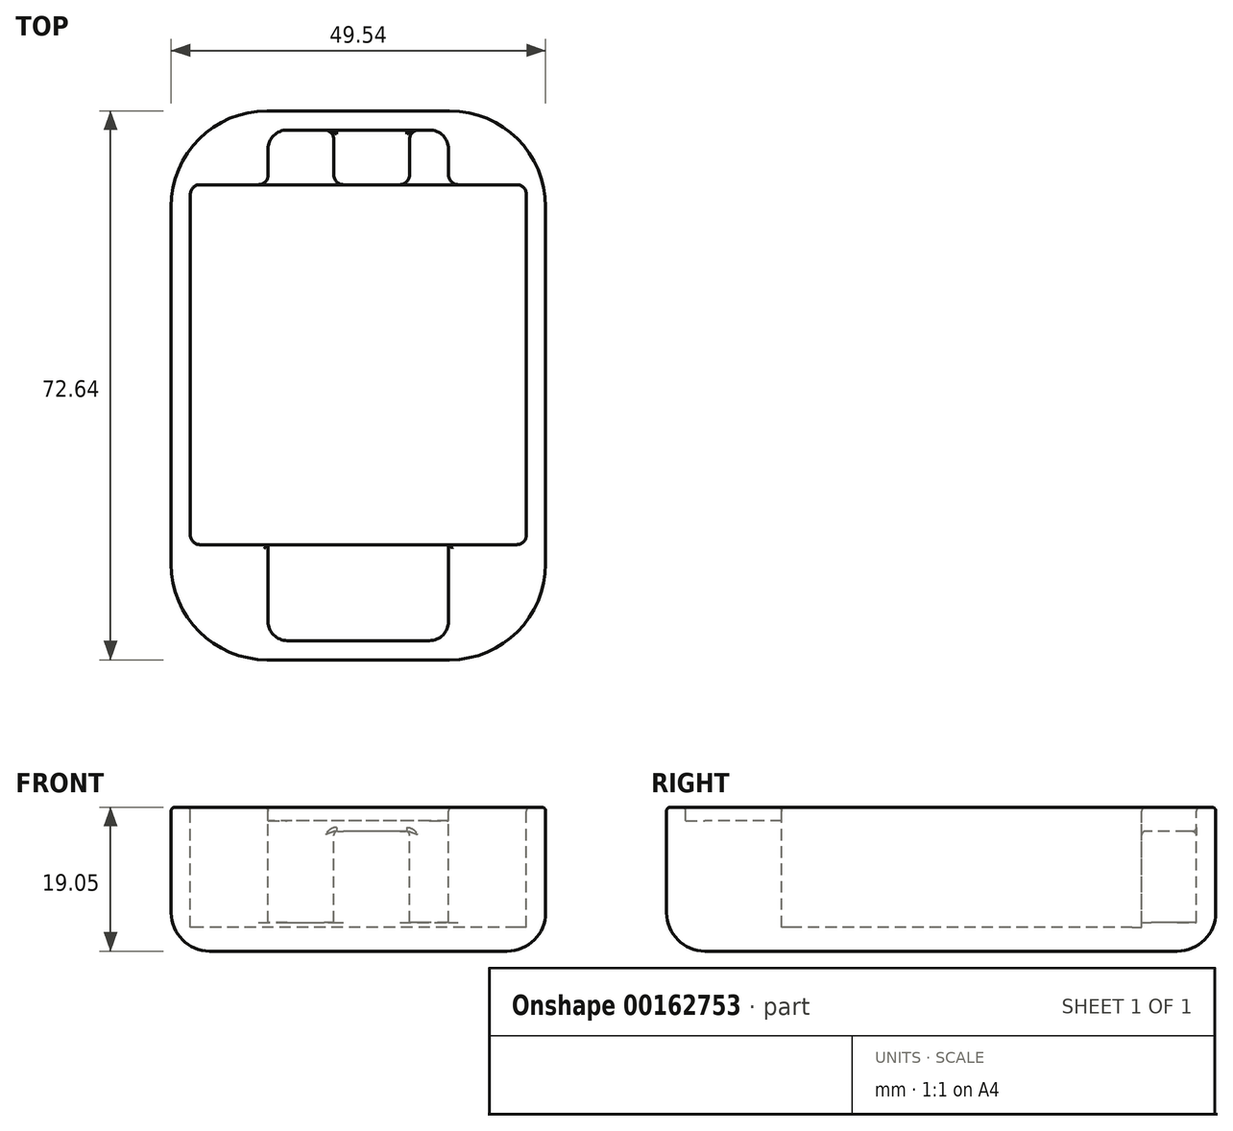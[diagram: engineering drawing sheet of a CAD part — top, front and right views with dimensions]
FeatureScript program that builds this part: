
annotation { "Feature Type Name" : "Feature", "Feature Type Description" : "" }
export const myFeature = defineFeature(function(context is Context, id is Id, definition is map)
    precondition{}
    {
        {
            var Q0;
            Q0=qCreatedBy(makeId("Top.planeOp"),FACE);
            var sketch = newSketch(context, id + "F0", { "sketchPlane" : qUnion([Q0])});
            skLineSegment(sketch, "E0.bottom", {"start": v(11.94, 33.78) * mm, "end": v(-11.94, 33.78) * mm});
            skLineSegment(sketch, "E0.top", {"start": v(11.94, -33.78) * mm, "end": v(-11.94, -33.78) * mm});
            skLineSegment(sketch, "E0.left", {"start": v(11.94, 33.78) * mm, "end": v(11.94, -33.78) * mm});
            skLineSegment(sketch, "E0.right", {"start": v(-11.94, 33.78) * mm, "end": v(-11.94, -33.78) * mm});
            skPoint(sketch, "E0.middle", {"position": v(0, 0) * mm});
            skLineSegment(sketch, "E1.bottom", {"start": v(22.22, 26.54) * mm, "end": v(-22.23, 26.54) * mm});
            skLineSegment(sketch, "E1.top", {"start": v(22.23, -21.08) * mm, "end": v(-22.22, -21.08) * mm});
            skLineSegment(sketch, "E1.left", {"start": v(22.23, 26.54) * mm, "end": v(22.23, -21.08) * mm});
            skLineSegment(sketch, "E1.right", {"start": v(-22.23, 26.54) * mm, "end": v(-22.23, -21.08) * mm});
            skPoint(sketch, "E1.middle", {"position": v(0, 2.73) * mm});
            skLineSegment(sketch, "E2.bottom", {"start": v(24.76, 36.32) * mm, "end": v(-24.77, 36.32) * mm});
            skLineSegment(sketch, "E2.top", {"start": v(24.77, -36.32) * mm, "end": v(-24.76, -36.32) * mm});
            skLineSegment(sketch, "E2.left", {"start": v(24.76, 36.32) * mm, "end": v(24.77, -36.32) * mm});
            skLineSegment(sketch, "E2.right", {"start": v(-24.77, 36.32) * mm, "end": v(-24.76, -36.32) * mm});
            skSolve(sketch);
        }
        {
            var Q0;
            {var subQ10=sQuery(id+"F0.wireOp",EDGE,"E0.bottom");Q0=makeQuery(id+"F0.imprint","IMPRINT",FACE,{"disambiguationData":[TD([[makeQuery(id+"F0.imprint","IMPRINT",EDGE,{"derivedFrom":subQ10}),-1.0]])]});}
            var Q1;
            {var subQ0=sQuery(id+"F0.wireOp",EDGE,"E0.bottom");Q1=makeQuery(id+"F0.imprint","IMPRINT",FACE,{"disambiguationData":[TD([[makeQuery(id+"F0.imprint","IMPRINT",EDGE,{"derivedFrom":subQ0}),1.0]])]});}
            var Q2;
            {var subQ5=sQuery(id+"F0.wireOp",EDGE,"E1.right");Q2=makeQuery(id+"F0.imprint","IMPRINT",FACE,{"disambiguationData":[TD([[makeQuery(id+"F0.imprint","IMPRINT",EDGE,{"derivedFrom":subQ5}),1.0]])]});}
            var Q3;
            {var subQ0=sQuery(id+"F0.wireOp",EDGE,"E1.bottom");var subQ1=sQuery(id+"F0.wireOp",EDGE,"E0.left");var subQ2=makeQuery(id+"F0.imprint","INTERSECT",VERTEX,{"derivedFrom":[subQ1,subQ0]});Q3=makeQuery(id+"F0.imprint","IMPRINT",FACE,{"disambiguationData":[TD([[makeQuery(id+"F0.imprint","IMPRINT",EDGE,{"disambiguationData":[TD([[subQ2,-1.0]])],"derivedFrom":subQ1}),-1.0]])]});}
            var Q4;
            {var subQ5=sQuery(id+"F0.wireOp",EDGE,"E1.left");Q4=makeQuery(id+"F0.imprint","IMPRINT",FACE,{"disambiguationData":[TD([[makeQuery(id+"F0.imprint","IMPRINT",EDGE,{"derivedFrom":subQ5}),-1.0]])]});}
            var Q5;
            {var subQ0=sQuery(id+"F0.wireOp",EDGE,"E0.top");Q5=makeQuery(id+"F0.imprint","IMPRINT",FACE,{"disambiguationData":[TD([[makeQuery(id+"F0.imprint","IMPRINT",EDGE,{"derivedFrom":subQ0}),-1.0]])]});}
            var Q6;
            Q6=sQuery(id+"F0.wireOp",EDGE,"E2.bottom");
            var Q7;
            Q7=sQuery(id+"F0.wireOp",EDGE,"E2.right");
            var Q8;
            Q8=sQuery(id+"F0.wireOp",EDGE,"E2.left");
            var Q9;
            Q9=sQuery(id+"F0.wireOp",EDGE,"E2.top");
            extrude(context, id + "F1", {"entities" : qUnion([Q0, Q1, Q2, Q3, Q4, Q5]), "surfaceEntities" : qUnion([Q6, Q7, Q8, Q9]), "oppositeDirection" : true, "depth" : 19.05 * mm});
        }
        {
            var Q0;
            {var subQ5=sQuery(id+"F0.wireOp",EDGE,"E1.right");Q0=makeQuery(id+"F0.imprint","IMPRINT",FACE,{"disambiguationData":[TD([[makeQuery(id+"F0.imprint","IMPRINT",EDGE,{"derivedFrom":subQ5}),1.0]])]});}
            var Q1;
            {var subQ0=sQuery(id+"F0.wireOp",EDGE,"E1.bottom");var subQ1=sQuery(id+"F0.wireOp",EDGE,"E0.left");var subQ2=makeQuery(id+"F0.imprint","INTERSECT",VERTEX,{"derivedFrom":[subQ1,subQ0]});Q1=makeQuery(id+"F0.imprint","IMPRINT",FACE,{"disambiguationData":[TD([[makeQuery(id+"F0.imprint","IMPRINT",EDGE,{"disambiguationData":[TD([[subQ2,-1.0]])],"derivedFrom":subQ1}),-1.0]])]});}
            var Q2;
            {var subQ5=sQuery(id+"F0.wireOp",EDGE,"E1.left");Q2=makeQuery(id+"F0.imprint","IMPRINT",FACE,{"disambiguationData":[TD([[makeQuery(id+"F0.imprint","IMPRINT",EDGE,{"derivedFrom":subQ5}),-1.0]])]});}
            extrude(context, id + "F2", {"entities" : qUnion([Q0, Q1, Q2]), "operationType" : NewBodyOperationType.REMOVE, "oppositeDirection" : true, "depth" : 15.88 * mm});
        }
        {
            var Q0;
            {var subQ0=sQuery(id+"F0.wireOp",EDGE,"E0.bottom");Q0=makeQuery(id+"F0.imprint","IMPRINT",FACE,{"disambiguationData":[TD([[makeQuery(id+"F0.imprint","IMPRINT",EDGE,{"derivedFrom":subQ0}),1.0]])]});}
            var Q1;
            {var subQ0=sQuery(id+"F0.wireOp",EDGE,"E0.top");Q1=makeQuery(id+"F0.imprint","IMPRINT",FACE,{"disambiguationData":[TD([[makeQuery(id+"F0.imprint","IMPRINT",EDGE,{"derivedFrom":subQ0}),-1.0]])]});}
            extrude(context, id + "F3", {"entities" : qUnion([Q0, Q1]), "operationType" : NewBodyOperationType.REMOVE, "oppositeDirection" : true, "depth" : 1.78 * mm});
        }
        {
            var Q0;
            {var subQ0=sQuery(id+"F0.wireOp",EDGE,"E0.bottom");Q0=makeQuery(id+"F0.imprint","IMPRINT",FACE,{"disambiguationData":[TD([[makeQuery(id+"F0.imprint","IMPRINT",EDGE,{"derivedFrom":subQ0}),1.0]])]});}
            extrude(context, id + "F4", {"entities" : qUnion([Q0]), "operationType" : NewBodyOperationType.REMOVE, "oppositeDirection" : true, "depth" : 3.17 * mm});
        }
        {
            var Q0;
            {var subQ0=sQuery(id+"F0.wireOp",EDGE,"E1.bottom");var subQ1=sQuery(id+"F0.wireOp",EDGE,"E0.left");var subQ2=makeQuery(id+"F0.imprint","INTERSECT",VERTEX,{"derivedFrom":[subQ1,subQ0]});Q0=makeQuery(id+"F0.imprint","IMPRINT",FACE,{"disambiguationData":[TD([[makeQuery(id+"F0.imprint","IMPRINT",EDGE,{"disambiguationData":[TD([[subQ2,-1.0]])],"derivedFrom":subQ1}),-1.0]])]});}
            var sketch = newSketch(context, id + "F5", { "sketchPlane" : qUnion([Q0])});
            skLineSegment(sketch, "E3.bottom", {"start": v(-11.94, 33.78) * mm, "end": v(-3.24, 33.78) * mm});
            skLineSegment(sketch, "E3.top", {"start": v(-11.94, 18.88) * mm, "end": v(-3.24, 18.88) * mm});
            skLineSegment(sketch, "E3.left", {"start": v(-11.94, 33.78) * mm, "end": v(-11.94, 18.88) * mm});
            skLineSegment(sketch, "E3.right", {"start": v(-3.24, 33.78) * mm, "end": v(-3.24, 18.88) * mm});
            skLineSegment(sketch, "E4.bottom", {"start": v(11.94, 33.78) * mm, "end": v(6.76, 33.78) * mm});
            skLineSegment(sketch, "E4.top", {"start": v(11.94, 22.64) * mm, "end": v(6.76, 22.64) * mm});
            skLineSegment(sketch, "E4.left", {"start": v(11.94, 33.78) * mm, "end": v(11.94, 22.64) * mm});
            skLineSegment(sketch, "E4.right", {"start": v(6.76, 33.78) * mm, "end": v(6.76, 22.64) * mm});
            skSolve(sketch);
        }
        {
            var Q0;
            Q0 = qSketchRegion(id + "F5", true);
            extrude(context, id + "F6", {"entities" : qUnion([Q0]), "operationType" : NewBodyOperationType.REMOVE, "oppositeDirection" : true, "depth" : 15.24 * mm});
        }
        {
            var Q0;
            Q0=makeQuery(id+"F1.opExtrude","SWEPT_EDGE",EDGE,{"disambiguationData":[OSD([sQuery(id+"F0.wireOp",EDGE,"E2.top"),sQuery(id+"F0.wireOp",EDGE,"E2.right")])]});
            var Q1;
            Q1=makeQuery(id+"F1.opExtrude","SWEPT_EDGE",EDGE,{"disambiguationData":[OSD([sQuery(id+"F0.wireOp",EDGE,"E2.top"),sQuery(id+"F0.wireOp",EDGE,"E2.left")])]});
            var Q2;
            Q2=makeQuery(id+"F1.opExtrude","SWEPT_EDGE",EDGE,{"disambiguationData":[OSD([sQuery(id+"F0.wireOp",EDGE,"E2.bottom"),sQuery(id+"F0.wireOp",EDGE,"E2.left")])]});
            var Q3;
            Q3=makeQuery(id+"F1.opExtrude","SWEPT_EDGE",EDGE,{"disambiguationData":[OSD([sQuery(id+"F0.wireOp",EDGE,"E2.bottom"),sQuery(id+"F0.wireOp",EDGE,"E2.right")])]});
            fillet(context, id + "F7", {"entities" : qUnion([Q0, Q1, Q2, Q3]), "radius" : 12.7 * mm, "tangentPropagation" : true, "allowEdgeOverflow" : false});
        }
        {
            var Q0;
            Q0=makeQuery(id+"F3.boolean.opBoolean","COPY",EDGE,{"derivedFrom":makeQuery(id+"F3.opExtrude","SWEPT_EDGE",EDGE,{"disambiguationData":[OSD([sQuery(id+"F0.wireOp",EDGE,"E0.bottom"),sQuery(id+"F0.wireOp",EDGE,"E0.left")])]})});
            var Q1;
            Q1=makeQuery(id+"F3.boolean.opBoolean","COPY",EDGE,{"derivedFrom":makeQuery(id+"F3.opExtrude","SWEPT_EDGE",EDGE,{"disambiguationData":[OSD([sQuery(id+"F0.wireOp",EDGE,"E0.bottom"),sQuery(id+"F0.wireOp",EDGE,"E0.right")])]})});
            var Q2;
            Q2=makeQuery(id+"F3.boolean.opBoolean","COPY",EDGE,{"derivedFrom":makeQuery(id+"F3.opExtrude","SWEPT_EDGE",EDGE,{"disambiguationData":[OSD([sQuery(id+"F0.wireOp",EDGE,"E0.top"),sQuery(id+"F0.wireOp",EDGE,"E0.right")])]})});
            var Q3;
            Q3=makeQuery(id+"F3.boolean.opBoolean","COPY",EDGE,{"derivedFrom":makeQuery(id+"F3.opExtrude","SWEPT_EDGE",EDGE,{"disambiguationData":[OSD([sQuery(id+"F0.wireOp",EDGE,"E0.top"),sQuery(id+"F0.wireOp",EDGE,"E0.left")])]})});
            fillet(context, id + "F8", {"entities" : qUnion([Q0, Q1, Q2, Q3]), "radius" : 2.54 * mm, "tangentPropagation" : true, "allowEdgeOverflow" : false});
        }
        {
            var Q0;
            {var subQ0=sQuery(id+"F0.wireOp",EDGE,"E2.left");var subQ1=sQuery(id+"F0.wireOp",EDGE,"E2.bottom");Q0=makeQuery(id+"F7.opFillet","BLEND_EDGE",EDGE,{"blendedFrom":[makeQuery(id+"F1.opExtrude","SWEPT_EDGE",EDGE,{"disambiguationData":[OSD([subQ1,subQ0])]}),makeQuery(id+"F1.opExtrude","CAP_FACE",FACE,{"disambiguationData":[OSD([subQ1,sQuery(id+"F0.wireOp",EDGE,"E2.top"),subQ0,sQuery(id+"F0.wireOp",EDGE,"E2.right")])],"isStart":false})],"blendedInto":[makeQuery(id+"F1.opExtrude","CAP_FACE",FACE,{"disambiguationData":[OSD([subQ1,sQuery(id+"F0.wireOp",EDGE,"E2.top"),subQ0,sQuery(id+"F0.wireOp",EDGE,"E2.right")])],"isStart":false})]});}
            fillet(context, id + "F9", {"entities" : qUnion([Q0]), "radius" : 5.08 * mm, "tangentPropagation" : true, "allowEdgeOverflow" : false});
        }
        {
            var Q0;
            Q0=makeQuery(id+"F2.boolean.opBoolean","COPY",EDGE,{"derivedFrom":makeQuery(id+"F2.opExtrude","SWEPT_EDGE",EDGE,{"disambiguationData":[OSD([sQuery(id+"F0.wireOp",EDGE,"E1.bottom"),sQuery(id+"F0.wireOp",EDGE,"E1.right")])]})});
            var Q1;
            Q1=makeQuery(id+"F2.boolean.opBoolean","COPY",EDGE,{"derivedFrom":makeQuery(id+"F2.opExtrude","SWEPT_EDGE",EDGE,{"disambiguationData":[OSD([sQuery(id+"F0.wireOp",EDGE,"E1.top"),sQuery(id+"F0.wireOp",EDGE,"E1.right")])]})});
            var Q2;
            Q2=makeQuery(id+"F2.boolean.opBoolean","COPY",EDGE,{"derivedFrom":makeQuery(id+"F2.opExtrude","SWEPT_EDGE",EDGE,{"disambiguationData":[OSD([sQuery(id+"F0.wireOp",EDGE,"E1.top"),sQuery(id+"F0.wireOp",EDGE,"E1.left")])]})});
            var Q3;
            Q3=makeQuery(id+"F2.boolean.opBoolean","COPY",EDGE,{"derivedFrom":makeQuery(id+"F2.opExtrude","SWEPT_EDGE",EDGE,{"disambiguationData":[OSD([sQuery(id+"F0.wireOp",EDGE,"E1.bottom"),sQuery(id+"F0.wireOp",EDGE,"E1.left")])]})});
            var Q4;
            Q4=makeQuery(id+"F3.boolean.opBoolean","COPY",EDGE,{"derivedFrom":makeQuery(id+"F3.opExtrude","SWEPT_EDGE",EDGE,{"disambiguationData":[OSD([sQuery(id+"F0.wireOp",EDGE,"E0.left"),sQuery(id+"F0.wireOp",EDGE,"E1.bottom")])]})});
            var Q5;
            Q5=makeQuery(id+"F3.boolean.opBoolean","COPY",EDGE,{"derivedFrom":makeQuery(id+"F3.opExtrude","SWEPT_EDGE",EDGE,{"disambiguationData":[OSD([sQuery(id+"F0.wireOp",EDGE,"E0.right"),sQuery(id+"F0.wireOp",EDGE,"E1.bottom")])]})});
            var Q6;
            Q6=makeQuery(id+"F3.boolean.opBoolean","COPY",EDGE,{"derivedFrom":makeQuery(id+"F3.opExtrude","SWEPT_EDGE",EDGE,{"disambiguationData":[OSD([sQuery(id+"F0.wireOp",EDGE,"E0.right"),sQuery(id+"F0.wireOp",EDGE,"E1.top")])]})});
            var Q7;
            Q7=makeQuery(id+"F3.boolean.opBoolean","COPY",EDGE,{"derivedFrom":makeQuery(id+"F3.opExtrude","SWEPT_EDGE",EDGE,{"disambiguationData":[OSD([sQuery(id+"F0.wireOp",EDGE,"E0.left"),sQuery(id+"F0.wireOp",EDGE,"E1.top")])]})});
            fillet(context, id + "F10", {"entities" : qUnion([Q0, Q1, Q2, Q3, Q4, Q5, Q6, Q7]), "radius" : 1.27 * mm, "tangentPropagation" : true, "allowEdgeOverflow" : false});
        }
        {
            var Q0;
            Q0=makeQuery(id+"F6.boolean.opBoolean","INTERSECT",EDGE,{"derivedFrom":[makeQuery(id+"F2.boolean.opBoolean","COPY",FACE,{"derivedFrom":makeQuery(id+"F2.opExtrude","SWEPT_FACE",FACE,{"disambiguationData":[OSD([sQuery(id+"F0.wireOp",EDGE,"E1.bottom")])]})}),makeQuery(id+"F6.opExtrude","SWEPT_FACE",FACE,{"disambiguationData":[OSD([sQuery(id+"F5.wireOp",EDGE,"E4.right")])]})]});
            var Q1;
            Q1=makeQuery(id+"F6.boolean.opBoolean","INTERSECT",EDGE,{"derivedFrom":[makeQuery(id+"F2.boolean.opBoolean","COPY",FACE,{"derivedFrom":makeQuery(id+"F2.opExtrude","SWEPT_FACE",FACE,{"disambiguationData":[OSD([sQuery(id+"F0.wireOp",EDGE,"E1.bottom")])]})}),makeQuery(id+"F6.opExtrude","SWEPT_FACE",FACE,{"disambiguationData":[OSD([sQuery(id+"F5.wireOp",EDGE,"E3.right")])]})]});
            var Q2;
            Q2=makeQuery(id+"F6.boolean.opBoolean","COPY",EDGE,{"derivedFrom":makeQuery(id+"F6.opExtrude","SWEPT_EDGE",EDGE,{"disambiguationData":[OSD([sQuery(id+"F5.wireOp",EDGE,"E3.bottom"),sQuery(id+"F5.wireOp",EDGE,"E3.right")])]})});
            var Q3;
            Q3=makeQuery(id+"F6.boolean.opBoolean","INTERSECT",EDGE,{"derivedFrom":[makeQuery(id+"F2.boolean.opBoolean","COPY",FACE,{"derivedFrom":makeQuery(id+"F2.opExtrude","SWEPT_FACE",FACE,{"disambiguationData":[OSD([sQuery(id+"F0.wireOp",EDGE,"E1.bottom")])]})}),makeQuery(id+"F6.opExtrude","SWEPT_FACE",FACE,{"disambiguationData":[OSD([sQuery(id+"F5.wireOp",EDGE,"E4.left")])]})]});
            var Q4;
            Q4=makeQuery(id+"F6.boolean.opBoolean","INTERSECT",EDGE,{"derivedFrom":[makeQuery(id+"F2.boolean.opBoolean","COPY",FACE,{"derivedFrom":makeQuery(id+"F2.opExtrude","SWEPT_FACE",FACE,{"disambiguationData":[OSD([sQuery(id+"F0.wireOp",EDGE,"E1.bottom")])]})}),makeQuery(id+"F6.opExtrude","SWEPT_FACE",FACE,{"disambiguationData":[OSD([sQuery(id+"F5.wireOp",EDGE,"E3.left")])]})]});
            var Q5;
            Q5=makeQuery(id+"F6.boolean.opBoolean","COPY",EDGE,{"derivedFrom":makeQuery(id+"F6.opExtrude","SWEPT_EDGE",EDGE,{"disambiguationData":[OSD([sQuery(id+"F5.wireOp",EDGE,"E4.bottom"),sQuery(id+"F5.wireOp",EDGE,"E4.right")])]})});
            fillet(context, id + "F11", {"entities" : qUnion([Q0, Q1, Q2, Q3, Q4, Q5]), "radius" : 1.27 * mm, "tangentPropagation" : true, "allowEdgeOverflow" : false});
        }
        {
            var Q0;
            Q0=makeQuery(id+"F1.opExtrude","CAP_FACE",FACE,{"disambiguationData":[OSD([sQuery(id+"F0.wireOp",EDGE,"E2.bottom"),sQuery(id+"F0.wireOp",EDGE,"E2.top"),sQuery(id+"F0.wireOp",EDGE,"E2.left"),sQuery(id+"F0.wireOp",EDGE,"E2.right")])],"isStart":true});
            var Q1;
            Q1=makeQuery(id+"F4.boolean.opBoolean","COPY",FACE,{"derivedFrom":makeQuery(id+"F4.opExtrude","CAP_FACE",FACE,{"disambiguationData":[OSD([sQuery(id+"F0.wireOp",EDGE,"E0.bottom"),sQuery(id+"F0.wireOp",EDGE,"E0.left"),sQuery(id+"F0.wireOp",EDGE,"E0.right"),sQuery(id+"F0.wireOp",EDGE,"E1.bottom")])],"isStart":false})});
            fillet(context, id + "F12", {"entities" : qUnion([Q0, Q1]), "radius" : 0.5 * mm, "tangentPropagation" : true, "allowEdgeOverflow" : false});
        }
    });
